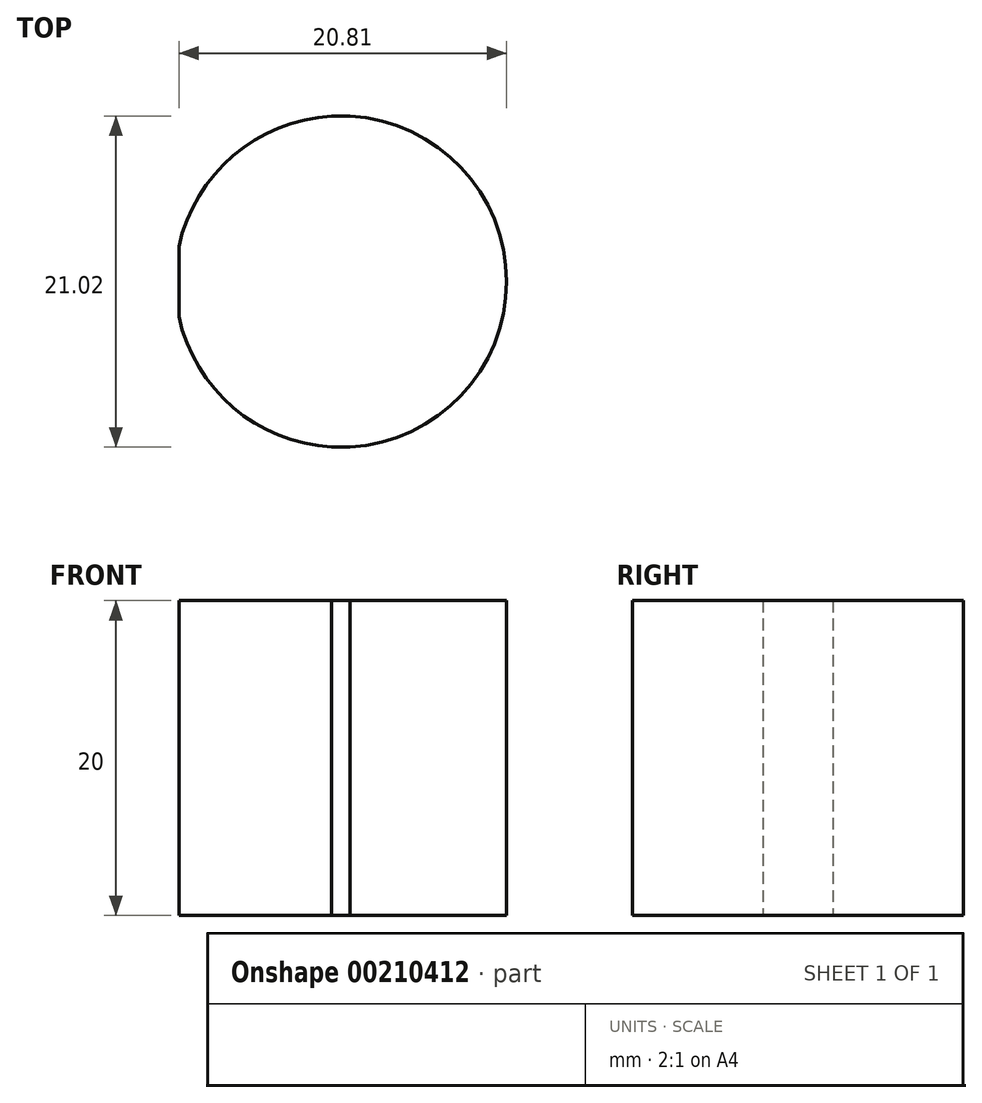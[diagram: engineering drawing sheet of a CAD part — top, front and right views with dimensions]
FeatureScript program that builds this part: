
annotation { "Feature Type Name" : "Feature", "Feature Type Description" : "" }
export const myFeature = defineFeature(function(context is Context, id is Id, definition is map)
    precondition{}
    {
        {
            var Q0;
            Q0=qCreatedBy(makeId("Top.planeOp"),FACE);
            var sketch = newSketch(context, id + "F0", { "sketchPlane" : qUnion([Q0])});
            skLineSegment(sketch, "E0.bottom", {"start": v(-36.74, 21.02) * mm, "end": v(33.76, 21.02) * mm});
            skLineSegment(sketch, "E0.top", {"start": v(-36.74, 0) * mm, "end": v(33.76, 0) * mm});
            skLineSegment(sketch, "E0.left", {"start": v(-36.74, 21.02) * mm, "end": v(-36.74, 0) * mm});
            skLineSegment(sketch, "E0.right", {"start": v(33.76, 21.02) * mm, "end": v(33.76, 0) * mm});
            skCircle(sketch, "E1", {"center": v(-26.45, 10.5) * mm, "radius": 10.52 * mm});
            skCircle(sketch, "E2", {"center": v(23.25, 10.5) * mm, "radius": 10.5 * mm});
            skPoint(sketch, "E3", {"position": v(-36.74, 10.5) * mm});
            skPoint(sketch, "E4", {"position": v(33.76, 10.5) * mm});
            skSolve(sketch);
        }
        {
            var Q0;
            {var subQ0=sQuery(id+"F0.wireOp",EDGE,"E1");var subQ1=sQuery(id+"F0.wireOp",EDGE,"E0.bottom");var subQ2=makeQuery(id+"F0.imprint","INTERSECT",VERTEX,{"disambiguationData":[OD(1.0)],"derivedFrom":[subQ1,subQ0]});Q0=makeQuery(id+"F0.imprint","IMPRINT",FACE,{"disambiguationData":[TD([[makeQuery(id+"F0.imprint","IMPRINT",EDGE,{"disambiguationData":[TD([[subQ2,-1.0]])],"derivedFrom":subQ1}),-1.0]])]});}
            extrude(context, id + "F1", {"entities" : qUnion([Q0]), "depth" : 20 * mm});
        }
    });
